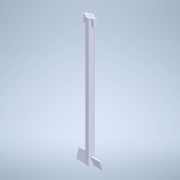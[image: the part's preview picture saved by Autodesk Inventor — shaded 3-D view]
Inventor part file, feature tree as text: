
AUTODESK INVENTOR PART (.ipt)
format: ipt  version: 2022 (Build 260153000, 153)  size: 144,896 bytes
history: mixed  units: mm
features: extrude x1, sketch x1, other x1, imported_body x1
ambient origin geometry x8: Origin, YZ Plane, XZ Plane, XY Plane, X Axis, Y Axis, Z Axis, Center Point
bodies: Solid1 (imported_parasolid)
feature tree (4):
  extrude  "Extrusion1"  Depth=1.0mm TaperAngle=0.0deg
  sketch  "Sketch1"  dims[d0=1.0mm d1=1.0mm d2=0.0mm]
  other  "Boss-Extrude4"
  imported_body  NMx_Import_Brep_tag  [imported B-rep: ~28 faces, bbox_mm=[16.0, 88.0, 4.0]]
